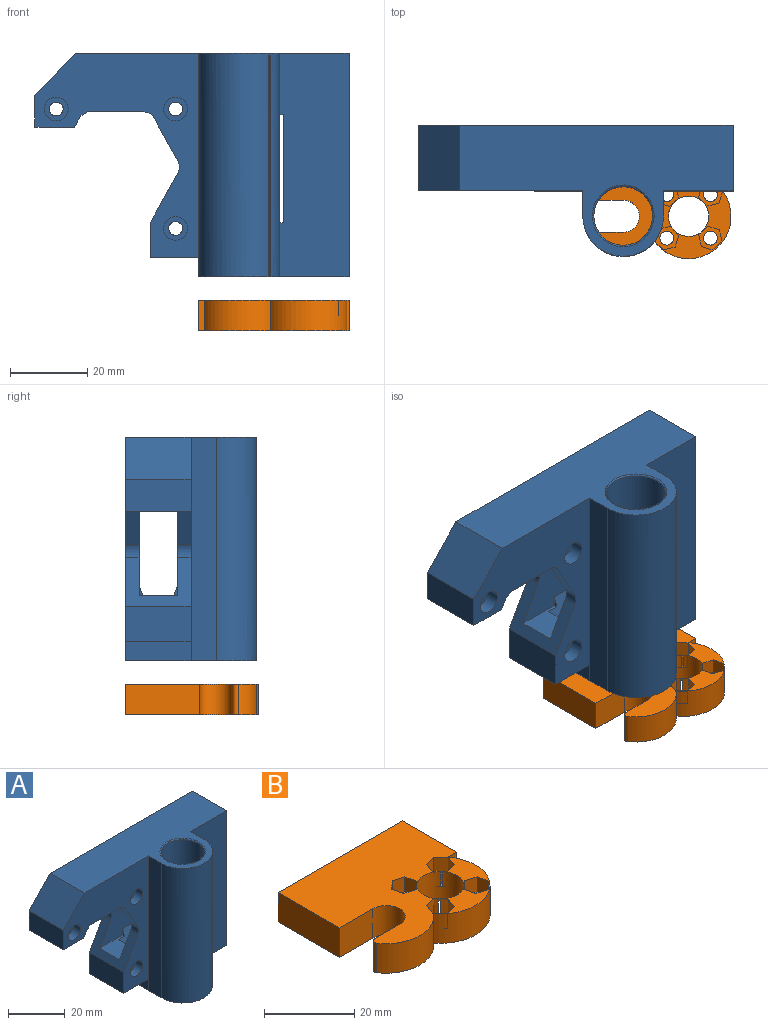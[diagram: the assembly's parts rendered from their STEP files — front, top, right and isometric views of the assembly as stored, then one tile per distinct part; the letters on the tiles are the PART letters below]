
ASSEMBLY  parts=2 mates=1
PART A: 77 faces, bbox 81.5x34x58 mm
  f0: cylinder r=10.47mm len=58mm, axis (0,0,1), area 1851.2mm2, adj f24,f25,f71,f72,f74,f75,f76
  f1: cylinder r=7.62mm len=57.6mm, axis (0,0,1), area 2698.4mm2, adj f24,f73,f74,f75,f76
  f2: plane 58x42.53mm, normal (0,-1,0), area 907.7mm2, adj f3,f15,f16,f17,f18,f20,f21,f22
  f3: cylinder r=3.5mm len=3.5mm, axis (0,1,0), area 12.4mm2, adj f2,f18,f20,f49
  f4: plane 10x3.25mm, normal (1,0,0), area 23.1mm2, adj f30,f48,f49,f52,f53,f68
  f5: plane 30.15x0.91mm, normal (0,-0.71,0.71), area 36.2mm2, adj f6,f8,f9,f64,f65
  f6: cylinder r=4.07mm len=29.1mm, axis (1,0,0), area 618.8mm2, adj f5,f7,f9,f65
  f7: plane 30.15x0.91mm, normal (0,0.71,0.71), area 36.2mm2, adj f6,f8,f9,f64,f65
  f8: plane 30.11x2.39mm, normal (0,0,1), area 70.9mm2, adj f5,f7,f9,f64
  f9: plane 58x17mm, normal (1,0,0), area 620mm2, adj f5,f6,f7,f8,f24,f25,f30,f32
  f10: plane 28x6.57mm, normal (1,0,0), area 108.5mm2, adj f30,f32,f35,f51,f52,f53
  f11: plane 28x6.57mm, normal (-1,0,0), area 108.5mm2, adj f30,f32,f35,f42,f43,f44
  f12: cylinder r=1.8mm len=13.5mm, axis (0,1,0), area 152.7mm2, adj f35,f41
  f13: cylinder r=1.8mm len=13.5mm, axis (0,1,0), area 152.7mm2, adj f35,f39
  f14: cylinder r=1.8mm len=13.5mm, axis (0,1,0), area 152.7mm2, adj f35,f37
  f15: plane 17x1.73mm, normal (0.5,0,-0.87), area 34mm2, adj f2,f16,f33,f35
  f16: plane 17x14.58mm, normal (0,0,-1), area 247.8mm2, adj f2,f15,f17,f35
  f17: cylinder r=3mm len=17mm, axis (0,1,0), area 54.2mm2, adj f2,f16,f18,f35
  f18: plane 17x11.05mm, normal (-0.87,0,-0.49), area 116.3mm2, adj f2,f3,f17,f19,f35,f49,f52,f68
  f19: cylinder r=3.5mm len=3.5mm, axis (0,1,0), area 12.4mm2, adj f18,f20,f35,f52
  f20: plane 17x12.59mm, normal (-0.87,0,0.49), area 132.8mm2, adj f2,f3,f19,f21,f35,f49,f52,f69
  f21: plane 17x9.14mm, normal (-1,0,0), area 155.4mm2, adj f2,f20,f22,f35
  f22: plane 17x12.5mm, normal (0,0,-1), area 212.5mm2, adj f2,f21,f23,f35
  f23: plane 17x5mm, normal (-1,0,0), area 85mm2, adj f2,f22,f24,f35
  f24: plane 39x33.98mm, normal (0,0,-1), area 786.5mm2, adj f0,f1,f2,f9,f23,f34,f35,f71
  f25: plane 71.05x33.98mm, normal (0,0,1), area 1314.6mm2, adj f0,f2,f9,f26,f34,f35,f71,f72
  f26: plane 17x10.95mm, normal (-0.72,0,0.69), area 257.3mm2, adj f2,f25,f27,f35
  f27: plane 17x8.3mm, normal (-1,0,0), area 141.1mm2, adj f2,f26,f28,f35
  f28: plane 17x10.21mm, normal (0,0,-1), area 173.6mm2, adj f2,f27,f33,f35
  f29: plane 28x6.57mm, normal (1,0,0), area 108.5mm2, adj f30,f32,f34,f48,f49,f50
  f30: plane 41.5x17mm, normal (0,0,-1), area 173.3mm2, adj f4,f9,f10,f11,f29,f31,f34,f35
  f31: plane 28x6.57mm, normal (-1,0,0), area 108.5mm2, adj f30,f32,f34,f45,f46,f47
  f32: plane 41.5x17mm, normal (0,0,1), area 256.4mm2, adj f9,f10,f11,f29,f31,f34,f35,f44
  f33: plane 17x2.97mm, normal (0.87,0,-0.5), area 58.3mm2, adj f2,f15,f28,f35
  f34: plane 58x18.03mm, normal (0,-1,0), area 1017.4mm2, adj f9,f24,f25,f29,f30,f31,f32,f72
  f35: plane 81.5x58mm, normal (0,1,0), area 3200.2mm2, adj f9,f10,f11,f12,f13,f14,f15,f16
  f36: cylinder r=3.1mm len=6.2mm, axis (0,-1,0), area 68.2mm2, adj f2,f37
  f37: plane 6.2x6.2mm, normal (0,-1,0), area 20mm2, adj f14,f36
  f38: cylinder r=3.1mm len=6.2mm, axis (0,-1,0), area 68.2mm2, adj f2,f39
  f39: plane 6.2x6.2mm, normal (0,-1,0), area 20mm2, adj f13,f38
  f40: cylinder r=3.1mm len=6.2mm, axis (0,-1,0), area 68.2mm2, adj f2,f41
  f41: plane 6.2x6.2mm, normal (0,-1,0), area 20mm2, adj f12,f40
  f42: plane 17x3.07mm, normal (0,-0.71,-0.71), area 73.8mm2, adj f9,f11,f30,f43
  f43: plane 19.31x17mm, normal (0,-1,0), area 328.3mm2, adj f9,f11,f42,f44
  f44: plane 17x5.62mm, normal (0,-0.94,0.34), area 101.7mm2, adj f9,f11,f32,f43
  f45: plane 17x5.62mm, normal (0,0.94,0.34), area 101.7mm2, adj f9,f31,f32,f46
  f46: plane 19.31x17mm, normal (0,1,0), area 328.3mm2, adj f9,f31,f45,f47
  f47: plane 17x3.07mm, normal (0,0.71,-0.71), area 73.8mm2, adj f9,f30,f31,f46
  f48: plane 23.5x3.07mm, normal (0,0.71,-0.71), area 102mm2, adj f4,f29,f30,f49
  f49: plane 31.95x22mm, normal (0,1,0), area 573.5mm2, adj f3,f4,f18,f20,f29,f48,f50,f67
  f50: plane 23.5x5.62mm, normal (0,0.94,0.34), area 131.9mm2, adj f29,f32,f49,f54,f67,f69
  f51: plane 23.5x5.62mm, normal (0,-0.94,0.34), area 131.9mm2, adj f10,f32,f52,f54,f69,f70
  f52: plane 31.95x22mm, normal (0,-1,0), area 573.5mm2, adj f4,f10,f18,f19,f20,f51,f53,f68
  f53: plane 23.5x3.07mm, normal (0,-0.71,-0.71), area 102mm2, adj f4,f10,f30,f52
  f54: plane 8.04x2.93mm, normal (1,0,0), area 20.4mm2, adj f32,f50,f51,f69
  f55: plane 30.15x0.91mm, normal (0,-0.71,0.71), area 36.2mm2, adj f9,f56,f58,f60,f61
  f56: cylinder r=4.07mm len=29.1mm, axis (1,0,0), area 618.8mm2, adj f9,f55,f57,f61
  f57: plane 30.15x0.91mm, normal (0,0.71,0.71), area 36.2mm2, adj f9,f56,f58,f60,f61
  f58: plane 30.11x2.39mm, normal (0,0,1), area 70.9mm2, adj f9,f55,f57,f60
  f59: cylinder r=5mm len=10mm, axis (-1,0,0), area 157.1mm2, adj f60,f62
  f60: cone r=5mm half-angle=13.6deg, axis (-1,0,0), area 85.3mm2, adj f55,f57,f58,f59,f61
  f61: plane 8.6x8.3mm, normal (-1,0,0), area 5.1mm2, adj f55,f56,f57,f60
  f62: plane 10x10mm, normal (1,0,0), area 78.5mm2, adj f59
  f63: cylinder r=5mm len=10mm, axis (1,0,0), area 157.1mm2, adj f64,f66
  f64: cone r=5mm half-angle=13.6deg, axis (-1,0,0), area 85.3mm2, adj f5,f7,f8,f63,f65
  f65: plane 8.6x8.3mm, normal (-1,0,0), area 5.1mm2, adj f5,f6,f7,f64
  f66: plane 10x10mm, normal (1,0,0), area 78.5mm2, adj f63
  f67: plane 2.69x0.98mm, normal (-1,0,0), area 1.3mm2, adj f49,f50,f69
  f68: plane 10x7.79mm, normal (0,0,-1), area 77.9mm2, adj f4,f18,f49,f52
  f69: plane 11.45x10mm, normal (0,0,1), area 90.3mm2, adj f20,f49,f50,f51,f52,f54,f67,f70
  f70: plane 2.69x0.98mm, normal (-1,0,0), area 1.3mm2, adj f51,f52,f69
  f71: plane 58x6.5mm, normal (-1,0,0), area 377mm2, adj f0,f2,f24,f25
  f72: plane 58x6.5mm, normal (1,0,0), area 377mm2, adj f0,f24,f25,f34
  f73: torus R=8.01mm, axis (0,0,-1), area 30.6mm2, adj f1,f25
  f74: plane 57.5x2.15mm, normal (-0.66,-0.75,0), area 164.7mm2, adj f0,f1,f24,f76
  f75: plane 57.5x2.15mm, normal (0.66,0.75,0), area 164.7mm2, adj f0,f1,f24,f76
  f76: plane 2.81x2.65mm, normal (0,0,-1), area 2.9mm2, adj f0,f1,f74,f75
PART B: 49 faces, bbox 39x34.5x8 mm
  f0: cylinder r=1.8mm len=4mm, axis (0,0,1), area 45.2mm2, adj f16,f48
  f1: cylinder r=1.8mm len=4mm, axis (0,0,1), area 45.2mm2, adj f16,f24
  f2: cylinder r=1.8mm len=4mm, axis (0,0,1), area 45.2mm2, adj f16,f32
  f3: cylinder r=1.8mm len=4mm, axis (0,0,1), area 45.2mm2, adj f16,f40
  f4: plane 39x34.5mm, normal (0,0,1), area 944.5mm2, adj f5,f6,f7,f8,f9,f10,f11,f12
  f5: plane 10.48x8mm, normal (0,-1,0), area 83.8mm2, adj f4,f6,f15,f16
  f6: cylinder r=4.2mm len=8.4mm, axis (0,0,1), area 105.6mm2, adj f4,f5,f7,f16
  f7: plane 8x7.92mm, normal (0,1,0), area 63.4mm2, adj f4,f6,f8,f16
  f8: cylinder r=1mm len=8mm, axis (0,0,1), area 17.2mm2, adj f4,f7,f9,f16
  f9: cylinder r=10.47mm len=16.93mm, axis (0,0,1), area 157.9mm2, adj f4,f8,f10,f16
  f10: cylinder r=11mm len=19.83mm, axis (0,0,1), area 275.9mm2, adj f4,f9,f11,f16
  f11: plane 8x2.65mm, normal (0,-1,0), area 21.2mm2, adj f4,f10,f12,f16
  f12: plane 17x8mm, normal (1,0,0), area 136mm2, adj f4,f11,f13,f16
  f13: plane 39x8mm, normal (0,1,0), area 312mm2, adj f4,f12,f15,f16
  f14: cylinder r=5.25mm len=10.5mm, axis (0,0,1), area 255.5mm2, adj f4,f16,f17,f23,f24,f25,f31,f32
  f15: plane 19.3x8mm, normal (-1,0,0), area 154.4mm2, adj f4,f5,f13,f16
  f16: plane 39x34.5mm, normal (0,0,-1), area 1008.6mm2, adj f0,f1,f2,f3,f5,f6,f7,f8
  f17: plane 4x0.74mm, normal (-0.68,0.74,0), area 4mm2, adj f4,f14,f18,f24
  f18: plane 4x3.1mm, normal (-0.98,-0.22,0), area 12.7mm2, adj f4,f17,f19,f24
  f19: plane 4x3.03mm, normal (-0.3,-0.95,0), area 12.7mm2, adj f4,f18,f20,f24
  f20: plane 4x2.33mm, normal (0.68,-0.74,0), area 12.7mm2, adj f4,f19,f21,f24
  f21: plane 4x3.1mm, normal (0.98,0.22,0), area 12.7mm2, adj f4,f20,f22,f24
  f22: plane 4x3.03mm, normal (0.3,0.95,0), area 12.7mm2, adj f4,f21,f23,f24
  f23: plane 4x1.21mm, normal (-0.68,0.74,0), area 6.6mm2, adj f4,f14,f22,f24
  f24: plane 6.2x6.06mm, normal (0,0,1), area 16mm2, adj f1,f14,f17,f18,f19,f20,f21,f22
  f25: plane 4x0.74mm, normal (0.74,0.68,0), area 4mm2, adj f4,f14,f26,f32
  f26: plane 4x3.1mm, normal (-0.22,0.98,0), area 12.7mm2, adj f4,f25,f27,f32
  f27: plane 4x3.03mm, normal (-0.95,0.3,0), area 12.7mm2, adj f4,f26,f28,f32
  f28: plane 4x2.33mm, normal (-0.74,-0.68,0), area 12.7mm2, adj f4,f27,f29,f32
  f29: plane 4x3.1mm, normal (0.22,-0.98,0), area 12.7mm2, adj f4,f28,f30,f32
  f30: plane 4x3.03mm, normal (0.95,-0.3,0), area 12.7mm2, adj f4,f29,f31,f32
  f31: plane 4x1.21mm, normal (0.74,0.68,0), area 6.6mm2, adj f4,f14,f30,f32
  f32: plane 6.2x6.06mm, normal (0,0,1), area 16mm2, adj f2,f14,f25,f26,f27,f28,f29,f30
  f33: plane 4x0.74mm, normal (0.68,-0.74,0), area 4mm2, adj f4,f14,f34,f40
  f34: plane 4x3.1mm, normal (0.98,0.22,0), area 12.7mm2, adj f4,f33,f35,f40
  f35: plane 4x3.03mm, normal (0.3,0.95,0), area 12.7mm2, adj f4,f34,f36,f40
  f36: plane 4x2.33mm, normal (-0.68,0.74,0), area 12.7mm2, adj f4,f35,f37,f40
  f37: plane 4x3.1mm, normal (-0.98,-0.22,0), area 12.7mm2, adj f4,f36,f38,f40
  f38: plane 4x3.03mm, normal (-0.3,-0.95,0), area 12.7mm2, adj f4,f37,f39,f40
  f39: plane 4x1.21mm, normal (0.68,-0.74,0), area 6.6mm2, adj f4,f14,f38,f40
  f40: plane 6.2x6.06mm, normal (0,0,1), area 16mm2, adj f3,f14,f33,f34,f35,f36,f37,f38
  f41: plane 4x0.74mm, normal (-0.74,-0.68,0), area 4mm2, adj f4,f14,f42,f48
  f42: plane 4x3.1mm, normal (0.22,-0.98,0), area 12.7mm2, adj f4,f41,f43,f48
  f43: plane 4x3.03mm, normal (0.95,-0.3,0), area 12.7mm2, adj f4,f42,f44,f48
  f44: plane 4x2.33mm, normal (0.74,0.68,0), area 12.7mm2, adj f4,f43,f45,f48
  f45: plane 4x3.1mm, normal (-0.22,0.98,0), area 12.7mm2, adj f4,f44,f46,f48
  f46: plane 4x3.03mm, normal (-0.95,0.3,0), area 12.7mm2, adj f4,f45,f47,f48
  f47: plane 4x1.21mm, normal (-0.74,-0.68,0), area 6.6mm2, adj f4,f14,f46,f48
  f48: plane 6.2x6.06mm, normal (0,0,1), area 16mm2, adj f0,f14,f41,f42,f43,f44,f45,f46
PLACE A t=(-4.92,15.93,-2.38)mm fixed
PLACE B rot(axis=(0,0,1),0deg) t=(4.5,-3.37,-40.99)mm
MATE slider B.f4 <-> A.f24  axis (0,0,1) through (30.62,15.93,-40.99)mm
